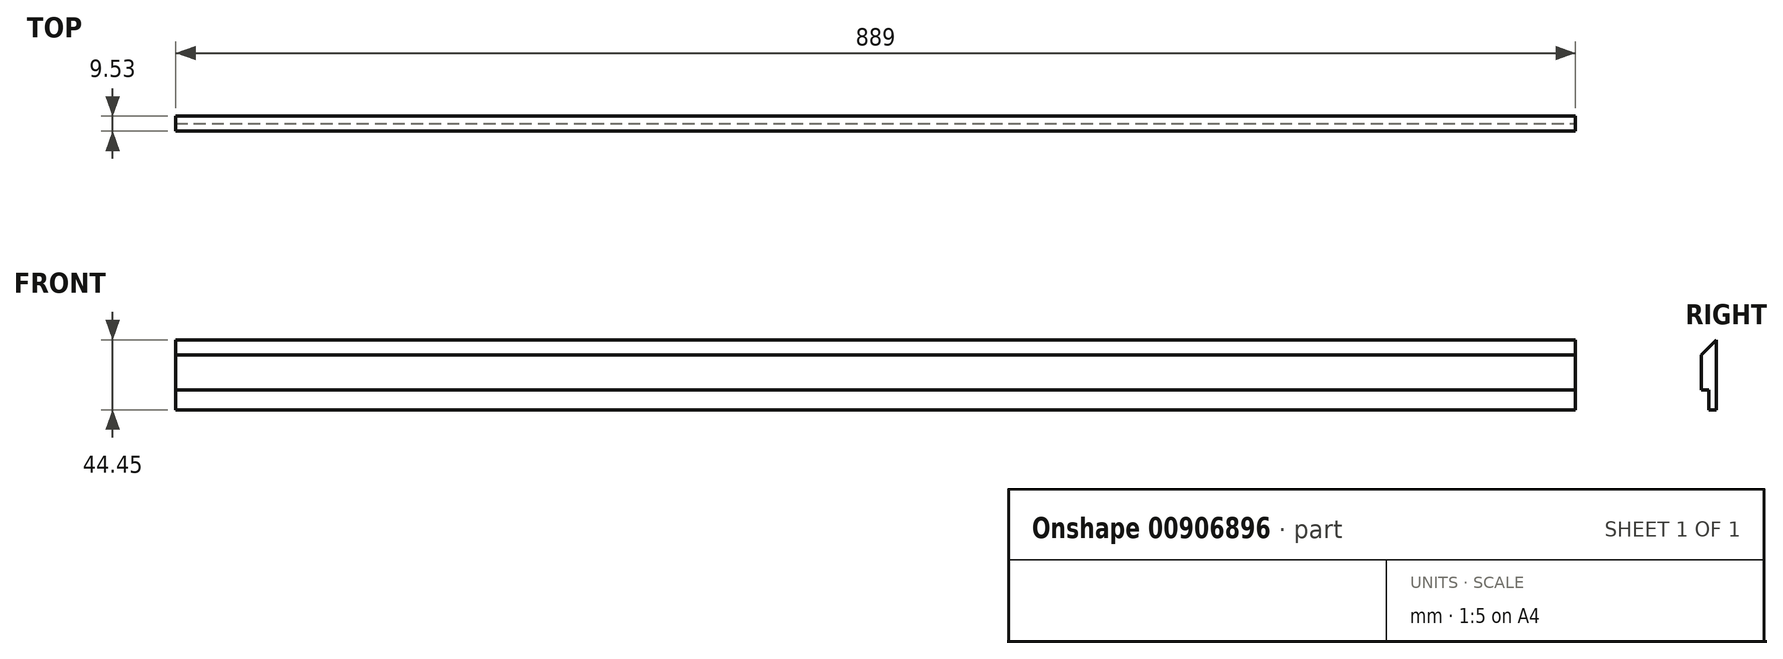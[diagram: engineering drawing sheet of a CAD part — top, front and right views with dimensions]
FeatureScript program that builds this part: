
annotation { "Feature Type Name" : "Feature", "Feature Type Description" : "" }
export const myFeature = defineFeature(function(context is Context, id is Id, definition is map)
    precondition{}
    {
        {
            var Q0;
            Q0=qCreatedBy(makeId("Right.planeOp"),FACE);
            var sketch = newSketch(context, id + "F0", { "sketchPlane" : qUnion([Q0])});
            skLineSegment(sketch, "E0", {"start": v(9.53, 0) * mm, "end": v(9.52, 44.45) * mm});
            skLineSegment(sketch, "E1", {"start": v(9.52, 44.45) * mm, "end": v(0, 34.93) * mm});
            skLineSegment(sketch, "E2", {"start": v(0, 34.93) * mm, "end": v(0, 0) * mm});
            skLineSegment(sketch, "E3", {"start": v(0, 0) * mm, "end": v(9.53, 0) * mm});
            skSolve(sketch);
        }
        {
            var Q0;
            Q0=makeQuery(id+"F0.imprint","IMPRINT",FACE,{"disambiguationData":[TD([[makeQuery(id+"F0.imprint","IMPRINT",EDGE,{"derivedFrom":sQuery(id+"F0.wireOp",EDGE,"E0")}),1.0]])]});
            extrude(context, id + "F1", {"entities" : qUnion([Q0]), "endBound" : BoundingType.SYMMETRIC, "depth" : 889 * mm, "offsetDistance" : 25.4 * mm});
        }
        {
            var Q0;
            Q0=makeQuery(id+"F1.opExtrude","CAP_FACE",FACE,{"disambiguationData":[OSD([sQuery(id+"F0.wireOp",EDGE,"E0"),sQuery(id+"F0.wireOp",EDGE,"E1"),sQuery(id+"F0.wireOp",EDGE,"E2"),sQuery(id+"F0.wireOp",EDGE,"E3")])],"isStart":false});
            var sketch = newSketch(context, id + "F2", { "sketchPlane" : qUnion([Q0])});
            skLineSegment(sketch, "E4", {"start": v(0, 0) * mm, "end": v(4.76, 0) * mm});
            skLineSegment(sketch, "E5", {"start": v(4.76, 0) * mm, "end": v(4.76, 12.7) * mm});
            skLineSegment(sketch, "E6", {"start": v(4.76, 12.7) * mm, "end": v(0, 12.7) * mm});
            skLineSegment(sketch, "E7", {"start": v(0, 12.7) * mm, "end": v(0, 0) * mm});
            skSolve(sketch);
        }
        {
            var Q0;
            Q0 = qSketchRegion(id + "F2", true);
            extrude(context, id + "F3", {"entities" : qUnion([Q0]), "operationType" : NewBodyOperationType.REMOVE, "endBound" : BoundingType.THROUGH_ALL, "oppositeDirection" : true, "depth" : 25.4 * mm, "offsetDistance" : 25.4 * mm});
        }
    });
